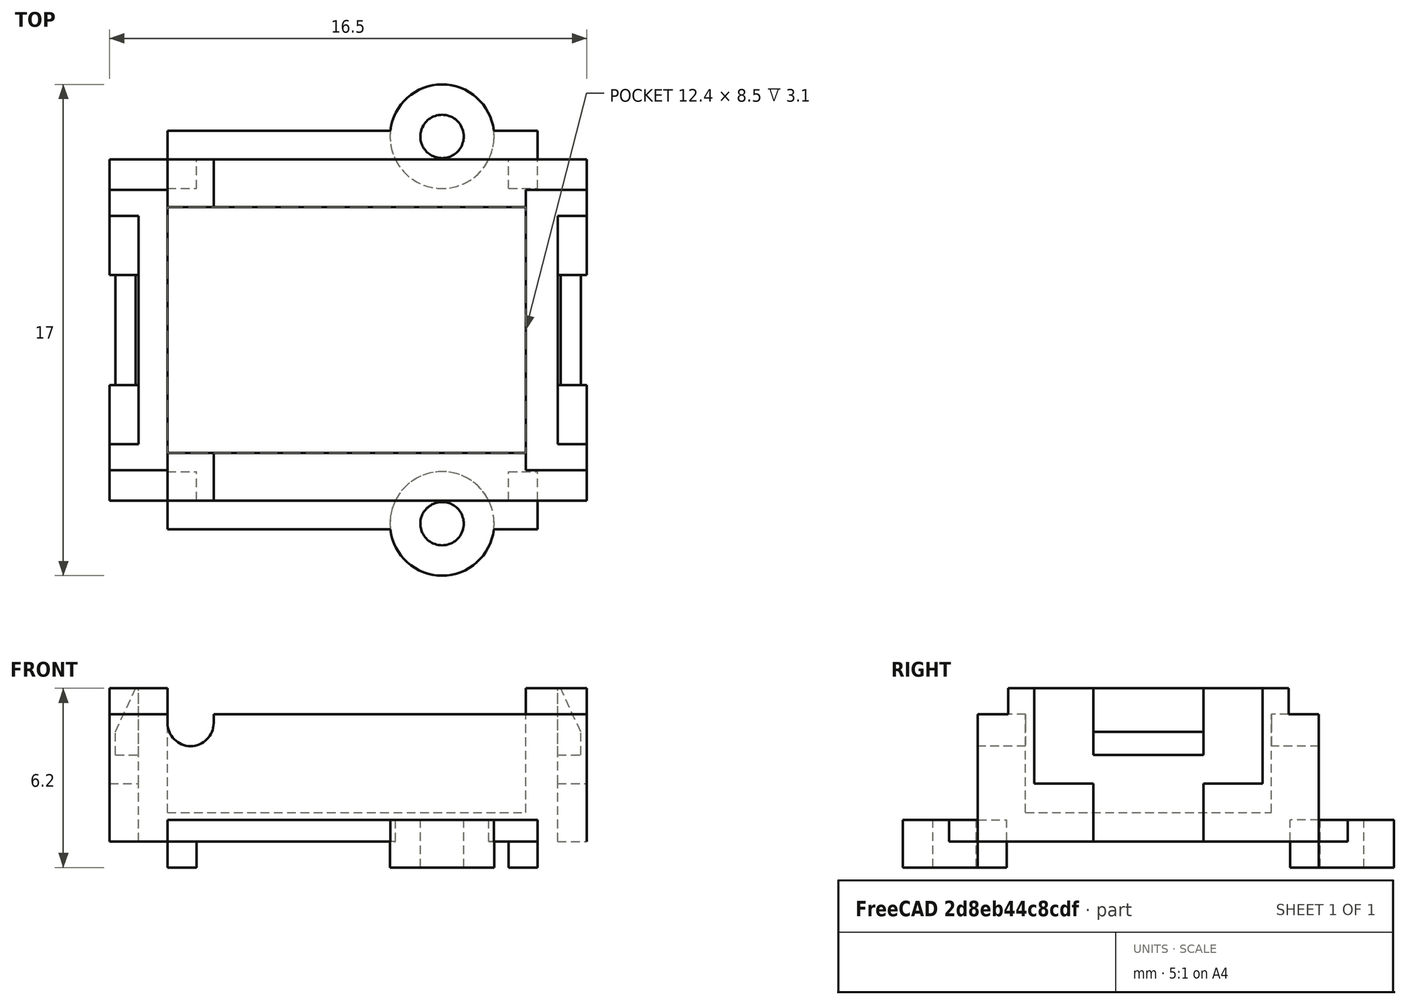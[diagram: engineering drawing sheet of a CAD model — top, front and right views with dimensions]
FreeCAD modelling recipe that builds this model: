
FCSTD DOCUMENT  (FreeCAD 0.18R4 (GitTag))
Label: bottom
License: All rights reserved
LicenseURL: http://en.wikipedia.org/wiki/All_rights_reserved
objects: Part::Box×20, Part::Cut×7, Part::MultiFuse×6, Part::Cylinder×5, Part::Chamfer×2, Part::Compound×1
note: 41 computed .brp shape members not serialized (recipe doc carries the construction recipe); baked Part::Feature solids carry a one-line shape summary decoded from their .brp

FEATURE [Part::Box] Box  label="Main"
  AttacherType = Attacher::AttachEngine3D
  Height = 5.3
  Length = 16.5
  Placement = pos=(0,-5.9,0.9) rot=(0,0,1;0rad)
  Width = 11.8
  expr: Placement.Base.y = -Width / 2
FEATURE [Part::Box] Box001  label="Cube001"
  AttacherType = Attacher::AttachEngine3D
  Height = 0.9
  Length = 1
  Placement = pos=(2,4.9,0) rot=(0,0,1;0rad)
  Width = 1
FEATURE [Part::Box] Box002  label="Cube002"
  AttacherType = Attacher::AttachEngine3D
  Height = 0.9
  Length = 1
  Placement = pos=(13.8,4.9,0) rot=(0,0,1;0rad)
  Width = 1
FEATURE [Part::Box] Box003  label="Cube003"
  AttacherType = Attacher::AttachEngine3D
  Height = 0.9
  Length = 1
  Placement = pos=(2,-5.9,0) rot=(0,0,1;0rad)
  Width = 1
FEATURE [Part::Box] Box004  label="Cube004"
  AttacherType = Attacher::AttachEngine3D
  Height = 0.9
  Length = 1
  Placement = pos=(13.8,-5.9,0) rot=(0,0,1;0rad)
  Width = 1
FEATURE [Part::Box] Box005  label="sk1"
  AttacherType = Attacher::AttachEngine3D
  Height = 0.75
  Length = 12.8
  Placement = pos=(2,5.9,0.9) rot=(0,0,1;0rad)
  Width = 1
FEATURE [Part::Box] Box006  label="sk2"
  AttacherType = Attacher::AttachEngine3D
  Height = 0.75
  Length = 12.8
  Placement = pos=(2,-6.9,0.9) rot=(0,0,1;0rad)
  Width = 1
FEATURE [Part::Cylinder] Cylinder
  Angle = 360
  AttacherType = Attacher::AttachEngine3D
  Height = 1.65
  Placement = pos=(11.5,-6.7,0) rot=(0,0,1;0rad)
  Radius = 1.8
FEATURE [Part::Cylinder] Cylinder001
  Angle = 360
  AttacherType = Attacher::AttachEngine3D
  Height = 1.65
  Placement = pos=(11.5,6.7,0) rot=(0,0,1;0rad)
  Radius = 1.8
FEATURE [Part::MultiFuse] Fusion
  Shapes = -> [Box006,Cylinder]
FEATURE [Part::MultiFuse] Fusion001
  Shapes = -> [Cylinder001,Box005]
FEATURE [Part::Cylinder] Cylinder002
  Angle = 360
  AttacherType = Attacher::AttachEngine3D
  Height = 10
  Placement = pos=(11.5,6.7,0) rot=(0,0,1;0rad)
  Radius = 0.75
FEATURE [Part::Cylinder] Cylinder003
  Angle = 360
  AttacherType = Attacher::AttachEngine3D
  Height = 10
  Placement = pos=(11.5,-6.7,0) rot=(0,0,1;0rad)
  Radius = 0.75
FEATURE [Part::Cut] Cut
  Base = -> Fusion
  Tool = -> Cylinder003
FEATURE [Part::Cut] Cut001
  Base = -> Fusion001
  Tool = -> Cylinder002
FEATURE [Part::Box] Box007  label="Cube005"
  AttacherType = Attacher::AttachEngine3D
  Height = 1
  Length = 16.5
  Placement = pos=(0,4.85,5.3) rot=(0,0,1;0rad)
  Width = 1.05
FEATURE [Part::Box] Box008  label="Cube006"
  AttacherType = Attacher::AttachEngine3D
  Height = 1
  Length = 16.5
  Placement = pos=(0,-5.9,5.3) rot=(0,0,1;0rad)
  Width = 1.05
FEATURE [Part::MultiFuse] Fusion002
  Shapes = -> [Box008,Box007]
FEATURE [Part::Cut] Cut002
  Base = -> Box
  Tool = -> Fusion002
FEATURE [Part::Box] Box009  label="Cube007"
  AttacherType = Attacher::AttachEngine3D
  Height = 5.3
  Length = 1
  Placement = pos=(0,-1.9,0.9) rot=(0,0,1;0rad)
  Width = 3.8
  expr: Placement.Base.y = -Width / 2
FEATURE [Part::Box] Box010  label="Cube008"
  AttacherType = Attacher::AttachEngine3D
  Height = 5.3
  Length = 1
  Placement = pos=(15.5,-1.9,0.9) rot=(0,0,1;0rad)
  Width = 3.8
  expr: Placement.Base.y = -Width / 2
FEATURE [Part::Box] Box011  label="Cube009"
  AttacherType = Attacher::AttachEngine3D
  Height = 3.3
  Length = 1
  Placement = pos=(15.5,-3.95,2.9) rot=(0,0,1;0rad)
  Width = 2.05
FEATURE [Part::Box] Box012  label="Cube010"
  AttacherType = Attacher::AttachEngine3D
  Height = 3.3
  Length = 1
  Placement = pos=(15.5,1.9,2.9) rot=(0,0,1;0rad)
  Width = 2.05
  expr: Placement.Base.y = 1.9
FEATURE [Part::Box] Box013  label="Cube011"
  AttacherType = Attacher::AttachEngine3D
  Height = 3.3
  Length = 1
  Placement = pos=(0,1.9,2.9) rot=(0,0,1;0rad)
  Width = 2.05
  expr: Placement.Base.y = 1.9
FEATURE [Part::Box] Box014  label="Cube012"
  AttacherType = Attacher::AttachEngine3D
  Height = 3.3
  Length = 1
  Placement = pos=(0,-3.95,2.9) rot=(0,0,1;0rad)
  Width = 2.05
FEATURE [Part::MultiFuse] Fusion003
  Shapes = -> [Box009,Box013,Box014,Box011,Box012,Box010]
FEATURE [Part::Cut] Cut003
  Base = -> Cut002
  Tool = -> Fusion003
FEATURE [Part::MultiFuse] Fusion004  label="Pods"
  Shapes = -> [Box004,Box002,Box003,Box001]
FEATURE [Part::Box] Box015  label="Cube013"
  AttacherType = Attacher::AttachEngine3D
  Height = 2.3
  Length = 0.8
  Placement = pos=(0.2,-1.9,3.9) rot=(0,0,1;0rad)
  Width = 3.8
  expr: Placement.Base.y = -Width / 2
FEATURE [Part::Box] Box016  label="Cube014"
  AttacherType = Attacher::AttachEngine3D
  Height = 2.3
  Length = 0.8
  Placement = pos=(15.5,-1.9,3.9) rot=(0,0,1;0rad)
  Width = 3.8
  expr: Placement.Base.y = -Width / 2
FEATURE [Part::Chamfer] Chamfer
  Base = -> Box015
  Edges = 1 edges: [Edge2 r1=1.5 r2=0.7]
FEATURE [Part::Chamfer] Chamfer001
  Base = -> Box016
  Edges = 1 edges: [Edge6 r1=1.5 r2=0.7]
FEATURE [Part::Box] Box017  label="Cube"
  AttacherType = Attacher::AttachEngine3D
  Height = 4.3
  Length = 12.4
  Placement = pos=(2,-4.25,1.9) rot=(0,0,1;0rad)
  Width = 8.5
  expr: Placement.Base.y = -Width / 2
FEATURE [Part::Cut] Cut004
  Base = -> Cut003
  Tool = -> Box017
FEATURE [Part::Cylinder] Cylinder004
  Angle = 360
  AttacherType = Attacher::AttachEngine3D
  Height = 20
  Placement = pos=(2.8,10,5) rot=(1,0,0;1.5708rad)
  Radius = 0.8
FEATURE [Part::Box] Box018  label="Cube015"
  AttacherType = Attacher::AttachEngine3D
  Height = 3
  Length = 1.6
  Placement = pos=(2,-10,5) rot=(0,0,1;0rad)
  Width = 20
FEATURE [Part::MultiFuse] Fusion005
  Shapes = -> [Box018,Cylinder004]
FEATURE [Part::Cut] Cut005
  Base = -> Cut004
  Tool = -> Fusion005
FEATURE [Part::Box] Box019  label="Cube016"
  AttacherType = Attacher::AttachEngine3D
  Height = 1
  Length = 12.3
  Placement = pos=(2.1,-4.85,5.3) rot=(0,0,1;0rad)
  Width = 9.7
  expr: Placement.Base.y = -Width / 2
FEATURE [Part::Cut] Cut006
  Base = -> Cut005
  Tool = -> Box019
FEATURE [Part::Compound] Compound
  Links = -> [Cut006,Cut,Cut001,Fusion004,Chamfer,Chamfer001]
